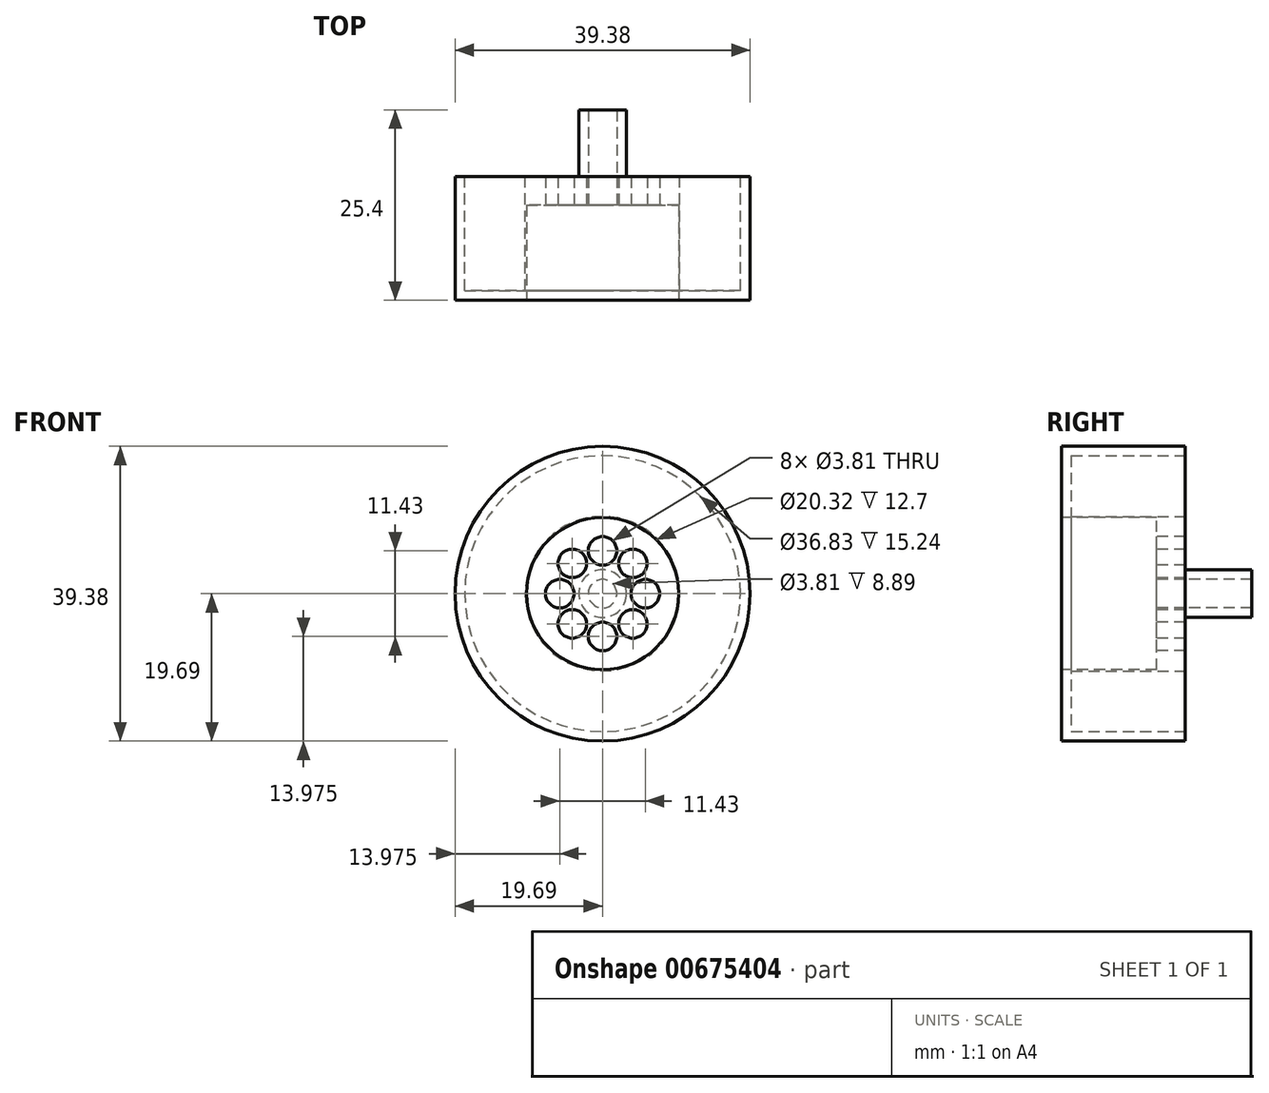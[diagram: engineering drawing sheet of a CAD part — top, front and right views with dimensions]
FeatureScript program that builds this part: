
annotation { "Feature Type Name" : "Feature", "Feature Type Description" : "" }
export const myFeature = defineFeature(function(context is Context, id is Id, definition is map)
    precondition{}
    {
        {
            var Q0;
            Q0=qCreatedBy(makeId("Front.planeOp"),FACE);
            var sketch = newSketch(context, id + "F0", { "sketchPlane" : qUnion([Q0])});
            skCircle(sketch, "E0", {"center": v(0, 0) * mm, "radius": 19.69 * mm});
            skSolve(sketch);
        }
        {
            var Q0;
            Q0=makeQuery(id+"F0.imprint","IMPRINT",FACE,{"disambiguationData":[TD([[makeQuery(id+"F0.imprint","IMPRINT",EDGE,{"derivedFrom":sQuery(id+"F0.wireOp",EDGE,"E0")}),1.0]])]});
            var sketch = newSketch(context, id + "F1", { "sketchPlane" : qUnion([Q0])});
            skCircle(sketch, "E1", {"center": v(0, 0) * mm, "radius": 10.16 * mm});
            skSolve(sketch);
        }
        {
            var Q0;
            Q0 = qSketchRegion(id + "F0", true);
            extrude(context, id + "F2", {"entities" : qUnion([Q0]), "oppositeDirection" : true, "depth" : 16.5 * mm, "offsetDistance" : 25.4 * mm});
        }
        {
            var Q0;
            Q0=makeQuery(id+"F1.imprint","IMPRINT",FACE,{"disambiguationData":[TD([[makeQuery(id+"F1.imprint","IMPRINT",EDGE,{"derivedFrom":sQuery(id+"F1.wireOp",EDGE,"E1")}),1.0]])]});
            extrude(context, id + "F3", {"entities" : qUnion([Q0]), "operationType" : NewBodyOperationType.REMOVE, "oppositeDirection" : true, "depth" : 12.7 * mm, "offsetDistance" : 25.4 * mm});
        }
        {
            var Q0;
            Q0=makeQuery(id+"F3.boolean.opBoolean","COPY",FACE,{"derivedFrom":makeQuery(id+"F3.opExtrude","CAP_FACE",FACE,{"disambiguationData":[OSD([sQuery(id+"F1.wireOp",EDGE,"E1")])],"isStart":false})});
            var sketch = newSketch(context, id + "F4", { "sketchPlane" : qUnion([Q0])});
            skCircle(sketch, "E2", {"center": v(0, 5.71) * mm, "radius": 1.9 * mm});
            skCircle(sketch, "E3.1.0", {"center": v(-4.04, 4.04) * mm, "radius": 1.9 * mm});
            skCircle(sketch, "E3.2.0", {"center": v(-5.71, 0) * mm, "radius": 1.9 * mm});
            skCircle(sketch, "E3.3.0", {"center": v(-4.04, -4.04) * mm, "radius": 1.9 * mm});
            skCircle(sketch, "E3.4.0", {"center": v(0, -5.71) * mm, "radius": 1.9 * mm});
            skCircle(sketch, "E3.5.0", {"center": v(4.04, -4.04) * mm, "radius": 1.9 * mm});
            skCircle(sketch, "E3.6.0", {"center": v(5.71, 0) * mm, "radius": 1.9 * mm});
            skCircle(sketch, "E3.7.0", {"center": v(4.04, 4.04) * mm, "radius": 1.9 * mm});
            skPoint(sketch, "E3.center", {"position": v(0, 0) * mm});
            skSolve(sketch);
        }
        {
            var Q0;
            Q0=makeQuery(id+"F4.imprint","IMPRINT",FACE,{"disambiguationData":[TD([[makeQuery(id+"F4.imprint","IMPRINT",EDGE,{"derivedFrom":sQuery(id+"F4.wireOp",EDGE,"E2")}),1.0]])]});
            var Q1;
            Q1=makeQuery(id+"F4.imprint","IMPRINT",FACE,{"disambiguationData":[TD([[makeQuery(id+"F4.imprint","IMPRINT",EDGE,{"derivedFrom":sQuery(id+"F4.wireOp",EDGE,"E3.7.0")}),1.0]])]});
            var Q2;
            Q2=makeQuery(id+"F4.imprint","IMPRINT",FACE,{"disambiguationData":[TD([[makeQuery(id+"F4.imprint","IMPRINT",EDGE,{"derivedFrom":sQuery(id+"F4.wireOp",EDGE,"E3.6.0")}),1.0]])]});
            var Q3;
            Q3=makeQuery(id+"F4.imprint","IMPRINT",FACE,{"disambiguationData":[TD([[makeQuery(id+"F4.imprint","IMPRINT",EDGE,{"derivedFrom":sQuery(id+"F4.wireOp",EDGE,"E3.5.0")}),1.0]])]});
            var Q4;
            Q4=makeQuery(id+"F4.imprint","IMPRINT",FACE,{"disambiguationData":[TD([[makeQuery(id+"F4.imprint","IMPRINT",EDGE,{"derivedFrom":sQuery(id+"F4.wireOp",EDGE,"E3.4.0")}),1.0]])]});
            var Q5;
            Q5=makeQuery(id+"F4.imprint","IMPRINT",FACE,{"disambiguationData":[TD([[makeQuery(id+"F4.imprint","IMPRINT",EDGE,{"derivedFrom":sQuery(id+"F4.wireOp",EDGE,"E3.3.0")}),1.0]])]});
            var Q6;
            Q6=makeQuery(id+"F4.imprint","IMPRINT",FACE,{"disambiguationData":[TD([[makeQuery(id+"F4.imprint","IMPRINT",EDGE,{"derivedFrom":sQuery(id+"F4.wireOp",EDGE,"E3.1.0")}),1.0]])]});
            var Q7;
            Q7=makeQuery(id+"F4.imprint","IMPRINT",FACE,{"disambiguationData":[TD([[makeQuery(id+"F4.imprint","IMPRINT",EDGE,{"derivedFrom":sQuery(id+"F4.wireOp",EDGE,"E3.2.0")}),1.0]])]});
            extrude(context, id + "F5", {"entities" : qUnion([Q0, Q1, Q2, Q3, Q4, Q5, Q6, Q7]), "operationType" : NewBodyOperationType.REMOVE, "oppositeDirection" : true, "depth" : 25.4 * mm, "offsetDistance" : 25.4 * mm});
        }
        {
            var Q0;
            Q0=makeQuery(id+"F2.opExtrude","CAP_FACE",FACE,{"disambiguationData":[OSD([sQuery(id+"F0.wireOp",EDGE,"E0")])],"isStart":false});
            var sketch = newSketch(context, id + "F6", { "sketchPlane" : qUnion([Q0])});
            skCircle(sketch, "E4", {"center": v(0, 0) * mm, "radius": 18.41 * mm});
            skCircle(sketch, "E5", {"center": v(0, 0) * mm, "radius": 10.32 * mm});
            skSolve(sketch);
        }
        {
            var Q0;
            Q0=makeQuery(id+"F6.imprint","IMPRINT",FACE,{"disambiguationData":[TD([[makeQuery(id+"F6.imprint","IMPRINT",EDGE,{"derivedFrom":sQuery(id+"F6.wireOp",EDGE,"E4")}),1.0]])]});
            extrude(context, id + "F7", {"entities" : qUnion([Q0]), "operationType" : NewBodyOperationType.REMOVE, "oppositeDirection" : true, "depth" : 15.24 * mm, "offsetDistance" : 25.4 * mm});
        }
        {
            var Q0;
            Q0=makeQuery(id+"F7.boolean.opBoolean","SPLIT",FACE,{"disambiguationData":[TD([makeQuery(id+"F5.boolean.opBoolean","COPY",FACE,{"derivedFrom":makeQuery(id+"F5.opExtrude","SWEPT_FACE",FACE,{"disambiguationData":[OSD([sQuery(id+"F4.wireOp",EDGE,"E2")])]})})])],"derivedFrom":makeQuery(id+"F2.opExtrude","CAP_FACE",FACE,{"disambiguationData":[OSD([sQuery(id+"F0.wireOp",EDGE,"E0")])],"isStart":false})});
            var sketch = newSketch(context, id + "F8", { "sketchPlane" : qUnion([Q0])});
            skCircle(sketch, "E6", {"center": v(0, 0) * mm, "radius": 3.18 * mm});
            skCircle(sketch, "E7", {"center": v(0, 0) * mm, "radius": 1.9 * mm});
            skSolve(sketch);
        }
        {
            var Q0;
            Q0=makeQuery(id+"F8.imprint","IMPRINT",FACE,{"disambiguationData":[TD([[makeQuery(id+"F8.imprint","IMPRINT",EDGE,{"derivedFrom":sQuery(id+"F8.wireOp",EDGE,"E6")}),1.0]])]});
            extrude(context, id + "F9", {"entities" : qUnion([Q0]), "operationType" : NewBodyOperationType.ADD, "depth" : 8.9 * mm, "offsetDistance" : 25.4 * mm});
        }
    });
